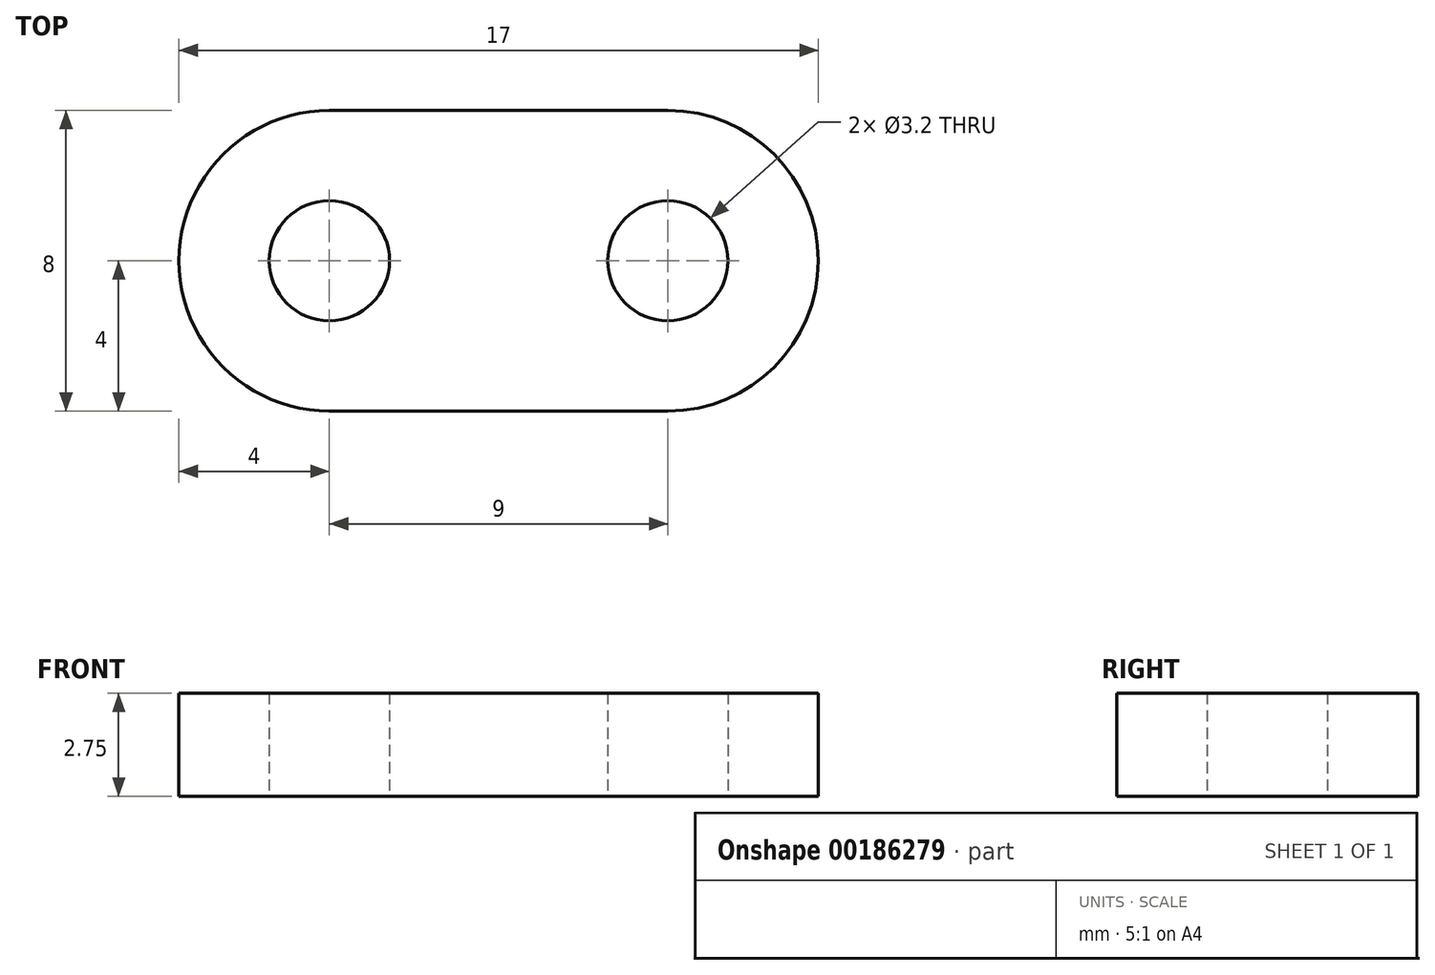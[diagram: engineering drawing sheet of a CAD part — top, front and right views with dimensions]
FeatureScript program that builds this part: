
annotation { "Feature Type Name" : "Feature", "Feature Type Description" : "" }
export const myFeature = defineFeature(function(context is Context, id is Id, definition is map)
    precondition{}
    {
        {
            var Q0;
            Q0=qCreatedBy(makeId("Top.planeOp"),FACE);
            var sketch = newSketch(context, id + "F0", { "sketchPlane" : qUnion([Q0])});
            skPoint(sketch, "E0", {"position": v(4.5, 0) * mm});
            skPoint(sketch, "E1", {"position": v(-4.5, 0) * mm});
            skCircle(sketch, "E2", {"center": v(4.5, 0) * mm, "radius": 1.6 * mm});
            skCircle(sketch, "E3", {"center": v(-4.5, 0) * mm, "radius": 1.6 * mm});
            skCircle(sketch, "E4", {"center": v(4.5, 0) * mm, "radius": 4 * mm});
            skCircle(sketch, "E5", {"center": v(-4.5, 0) * mm, "radius": 4 * mm});
            skPoint(sketch, "E6", {"position": v(4.5, -4) * mm});
            skPoint(sketch, "E7", {"position": v(-4.5, -4) * mm});
            skPoint(sketch, "E8", {"position": v(-4.5, 4) * mm});
            skPoint(sketch, "E9", {"position": v(4.5, 4) * mm});
            skLineSegment(sketch, "E10", {"start": v(-4.5, 4) * mm, "end": v(4.5, 4) * mm});
            skLineSegment(sketch, "E11", {"start": v(4.5, -4) * mm, "end": v(-4.5, -4) * mm});
            skSolve(sketch);
        }
        {
            var Q0;
            Q0=makeQuery(id+"F0.imprint","IMPRINT",FACE,{"disambiguationData":[TD([[makeQuery(id+"F0.imprint","IMPRINT",EDGE,{"derivedFrom":sQuery(id+"F0.wireOp",EDGE,"E3")}),-1.0]])]});
            var Q1;
            {var subQ3=sQuery(id+"F0.wireOp",EDGE,"E10");Q1=makeQuery(id+"F0.imprint","IMPRINT",FACE,{"disambiguationData":[TD([[makeQuery(id+"F0.imprint","IMPRINT",EDGE,{"derivedFrom":subQ3}),-1.0]])]});}
            var Q2;
            Q2=makeQuery(id+"F0.imprint","IMPRINT",FACE,{"disambiguationData":[TD([[makeQuery(id+"F0.imprint","IMPRINT",EDGE,{"derivedFrom":sQuery(id+"F0.wireOp",EDGE,"E2")}),-1.0]])]});
            extrude(context, id + "F1", {"entities" : qUnion([Q0, Q1, Q2]), "depth" : 2.75 * mm, "offsetDistance" : 25 * mm});
        }
    });
